# Revit family: Thorn LINN
name_source: partatom
category: Lighting Fixtures
revit_build: Autodesk Revit 2016 (Build: 20150220_1215(x64)
units: mm (PartAtom-declared; Revit-internal decimal feet)

## family parameters
Cut with Voids When Loaded = No
Host = Face
Light Source = Yes
OmniClass Number = 23.80.70.11
OmniClass Title = Luminaries for Internal Lighting
Part Type = Normal
Room Calculation Point = No
Round Connector Dimension = Use Diameter
Shared = No

## types (2) — shared parameters
Assembly Code = D5020200
Body = Thorn_Metal_Dark_Grey
Color Filter = 16777215
Cover = Thorn_Metal_Grey
Description = LED ceiling-recessed luminaire
Dimming Lamp Color Temperature Shift = <None>
Emit Shape Visible in Rendering = No
Lamp = LED
Manufacturer = Thorn Lighting
Reflector = Thorn_Glass_Self_llumination_Transparent
Tilt Angle = -90.00°
Voltage = 230 V
zero-valued in all types: Default Elevation

## per-type parameters (varying)
| type | Apparent Load | Emit from Rectangle Length | Emit from Rectangle Width | Height | Length | Model | Photometric Web File | URL | Width |
| LINN RCT | 11 VA | 70 mm | 197 mm | 91 mm  [stored 0.298556 ft] | 102 mm | 96262138 | 96262138_(STD).IES | www.thornlighting.com/96262138 | 229 mm |
| LINN SQ | 3 VA | 74 mm | 74 mm | 81 mm | 106 mm  [stored 0.347769 ft] | 96262124 | 96262124+96262129_(STD).IES | www.thornlighting.com/96262124 | 106 mm  [stored 0.347769 ft] |

note: [stored X ft] marks values corroborated as IEEE doubles in the binary element streams (Revit-internal decimal feet)

## geometry (parser evidence)
native form markers: Sweep x2
no freeform markers — native parametric forms only
